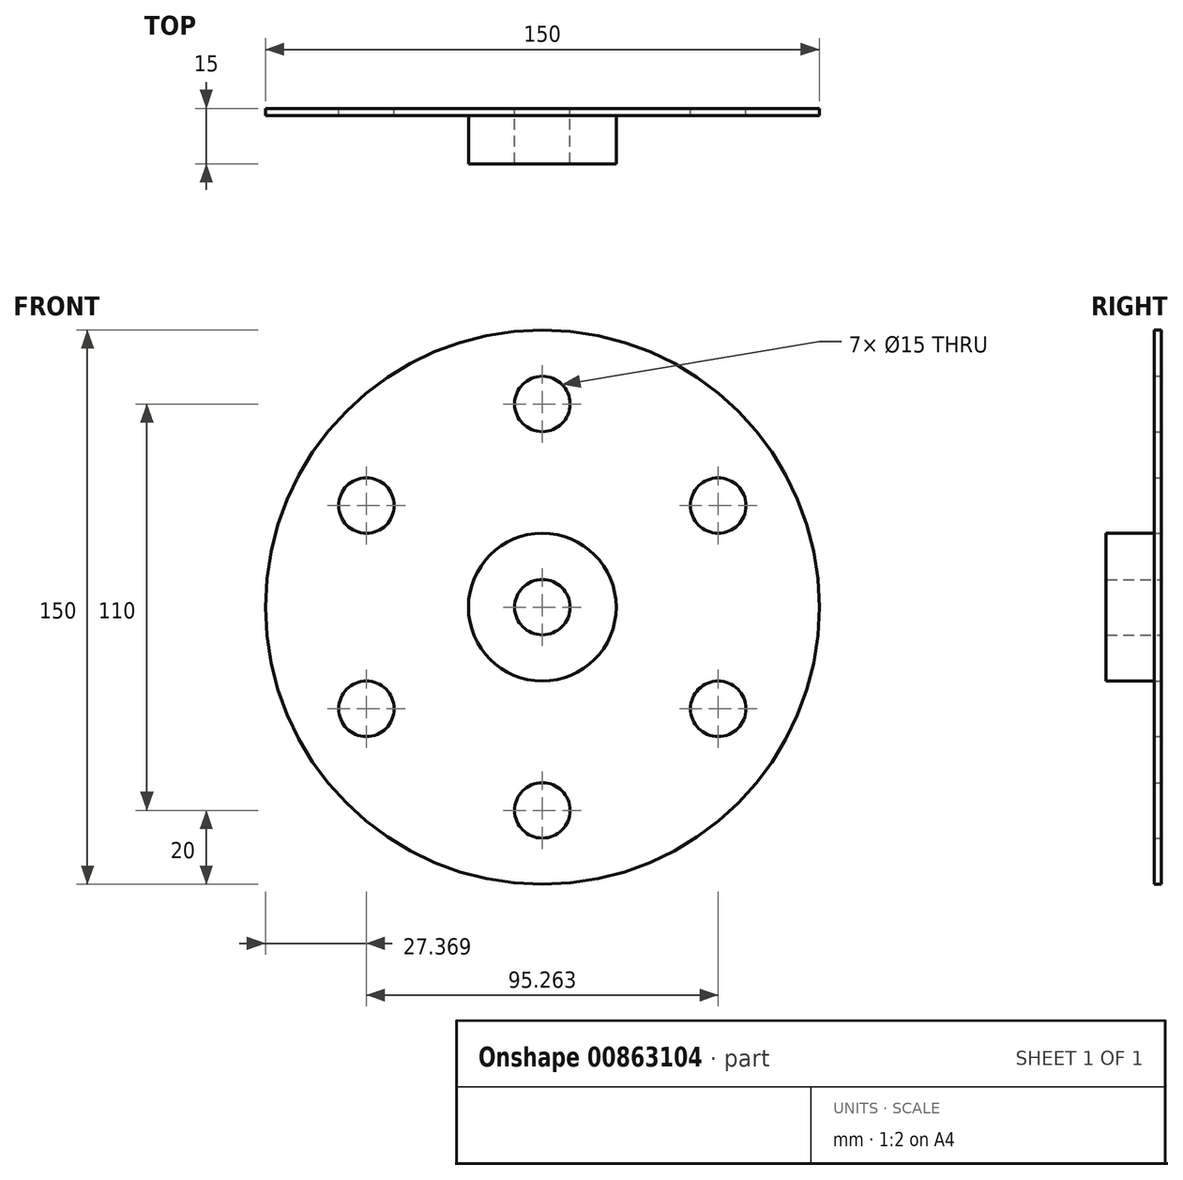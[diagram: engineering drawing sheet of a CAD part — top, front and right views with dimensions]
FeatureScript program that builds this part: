
annotation { "Feature Type Name" : "Feature", "Feature Type Description" : "" }
export const myFeature = defineFeature(function(context is Context, id is Id, definition is map)
    precondition{}
    {
        {
            var Q0;
            Q0=qCreatedBy(makeId("Front.planeOp"),FACE);
            var sketch = newSketch(context, id + "F0", { "sketchPlane" : qUnion([Q0])});
            skCircle(sketch, "E0", {"center": v(0, 0) * mm, "radius": 75 * mm});
            skCircle(sketch, "E1", {"center": v(0, 0) * mm, "radius": 20 * mm});
            skCircle(sketch, "E2", {"center": v(0, 55) * mm, "radius": 7.5 * mm});
            skCircle(sketch, "E3.1.0", {"center": v(-47.63, 27.5) * mm, "radius": 7.5 * mm});
            skCircle(sketch, "E3.2.0", {"center": v(-47.63, -27.5) * mm, "radius": 7.5 * mm});
            skCircle(sketch, "E3.3.0", {"center": v(0, -55) * mm, "radius": 7.5 * mm});
            skCircle(sketch, "E3.4.0", {"center": v(47.63, -27.5) * mm, "radius": 7.5 * mm});
            skCircle(sketch, "E3.5.0", {"center": v(47.63, 27.5) * mm, "radius": 7.5 * mm});
            skSolve(sketch);
        }
        {
            var Q0;
            Q0=makeQuery(id+"F0.imprint","IMPRINT",FACE,{"disambiguationData":[TD([[makeQuery(id+"F0.imprint","IMPRINT",EDGE,{"derivedFrom":sQuery(id+"F0.wireOp",EDGE,"E0")}),1.0]])]});
            extrude(context, id + "F1", {"entities" : qUnion([Q0]), "depth" : 2 * mm, "hasOffset" : true, "offsetDistance" : 2 * mm});
        }
        {
            var Q0;
            Q0=makeQuery(id+"F1.opExtrude","CAP_FACE",FACE,{"disambiguationData":[OSD([sQuery(id+"F0.wireOp",EDGE,"E0"),sQuery(id+"F0.wireOp",EDGE,"E1"),sQuery(id+"F0.wireOp",EDGE,"E2"),sQuery(id+"F0.wireOp",EDGE,"E3.1.0"),sQuery(id+"F0.wireOp",EDGE,"E3.2.0"),sQuery(id+"F0.wireOp",EDGE,"E3.3.0"),sQuery(id+"F0.wireOp",EDGE,"E3.4.0"),sQuery(id+"F0.wireOp",EDGE,"E3.5.0")])],"isStart":true});
            var sketch = newSketch(context, id + "F2", { "sketchPlane" : qUnion([Q0])});
            skCircle(sketch, "E4", {"center": v(0, 0) * mm, "radius": 7.5 * mm});
            skSolve(sketch);
        }
        {
            var Q0;
            Q0=makeQuery(id+"F2.imprint","IMPRINT",FACE,{"disambiguationData":[TD([[makeQuery(id+"F2.imprint","IMPRINT",EDGE,{"derivedFrom":sQuery(id+"F2.wireOp",EDGE,"E4")}),-1.0]])]});
            extrude(context, id + "F3", {"entities" : qUnion([Q0]), "operationType" : NewBodyOperationType.ADD, "oppositeDirection" : true, "depth" : 15 * mm, "offsetDistance" : 25 * mm});
        }
    });
